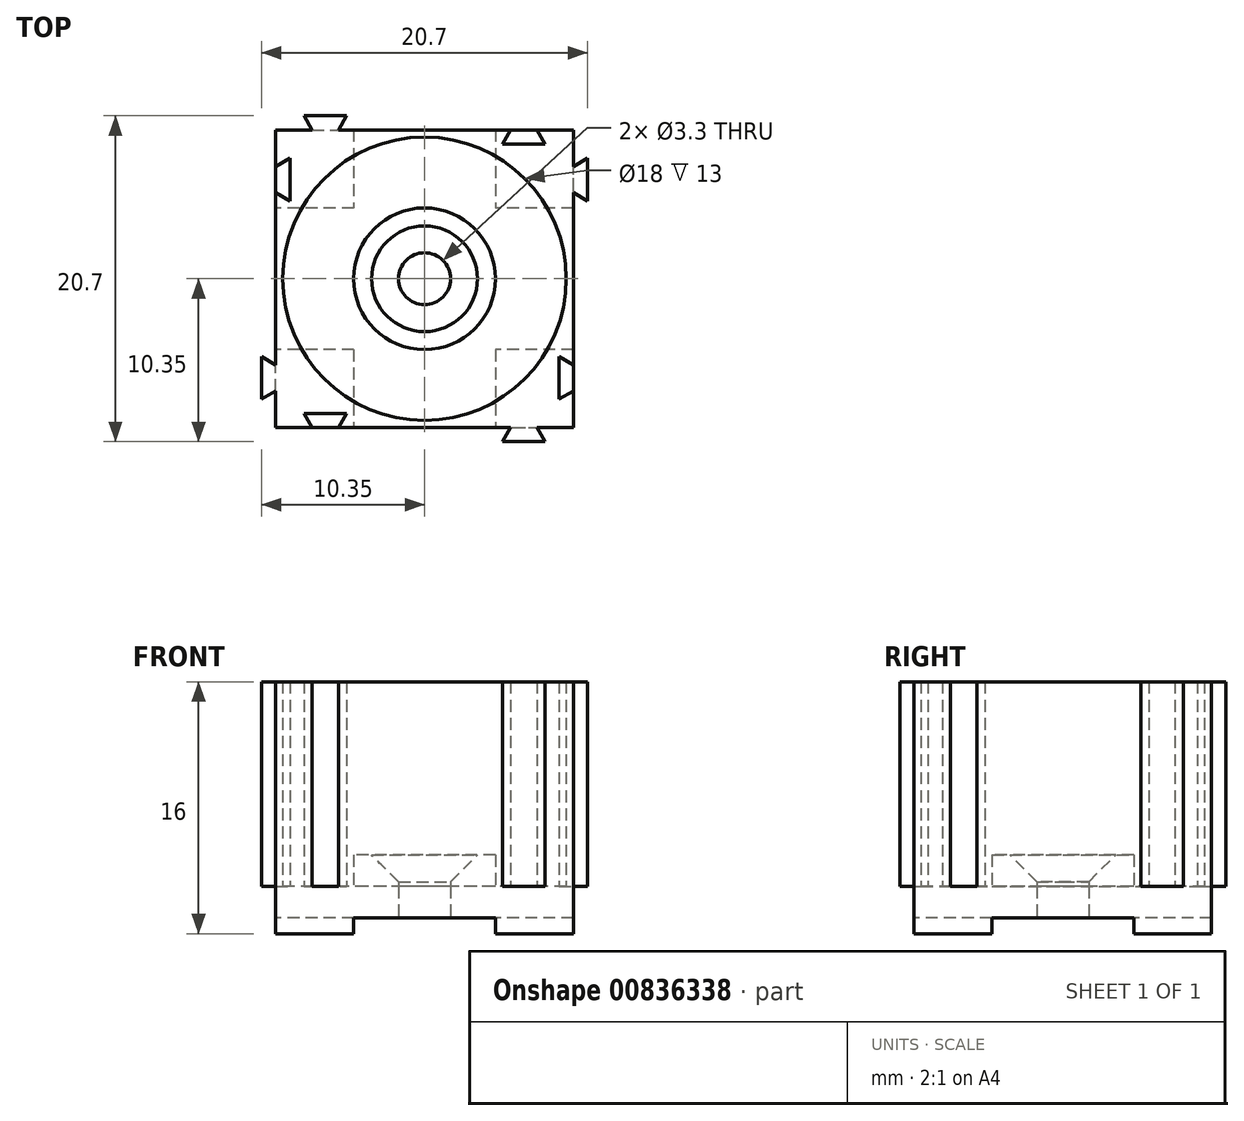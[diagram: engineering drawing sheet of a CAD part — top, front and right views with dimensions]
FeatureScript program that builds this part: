
annotation { "Feature Type Name" : "Feature", "Feature Type Description" : "" }
export const myFeature = defineFeature(function(context is Context, id is Id, definition is map)
    precondition{}
    {
        {
            assignVariable(context, id + "F0", {"name" : "Height", "anyValue" : 65});
        }
        {
            var Q0;
            Q0=qCreatedBy(makeId("Top.planeOp"),FACE);
            var sketch = newSketch(context, id + "F1", { "sketchPlane" : qUnion([Q0])});
            skCircle(sketch, "E0", {"center": v(0, 0) * mm, "radius": 9 * mm});
            skLineSegment(sketch, "E1.bottom", {"start": v(9.45, -9.45) * mm, "end": v(7.13, -9.45) * mm});
            skLineSegment(sketch, "E1.top", {"start": v(9.45, 9.45) * mm, "end": v(7.13, 9.45) * mm});
            skLineSegment(sketch, "E1.left", {"start": v(9.45, -9.45) * mm, "end": v(9.45, -7.13) * mm});
            skLineSegment(sketch, "E1.right", {"start": v(-9.45, -9.45) * mm, "end": v(-9.45, -7.13) * mm});
            skLineSegment(sketch, "E2", {"start": v(5.47, 9.45) * mm, "end": v(4.95, 8.55) * mm});
            skLineSegment(sketch, "E3", {"start": v(4.95, 8.55) * mm, "end": v(7.65, 8.55) * mm});
            skLineSegment(sketch, "E4", {"start": v(7.65, 8.55) * mm, "end": v(7.13, 9.45) * mm});
            skLineSegment(sketch, "E5", {"start": v(-7.13, 9.45) * mm, "end": v(-7.65, 10.35) * mm});
            skLineSegment(sketch, "E6", {"start": v(-7.65, 10.35) * mm, "end": v(-4.95, 10.35) * mm});
            skLineSegment(sketch, "E7", {"start": v(-4.95, 10.35) * mm, "end": v(-5.47, 9.45) * mm});
            skLineSegment(sketch, "E8", {"start": v(-6.3, 10.35) * mm, "end": v(-6.3, -11.64) * mm, "construction": true});
            skLineSegment(sketch, "E9", {"start": v(6.3, 8.55) * mm, "end": v(6.3, -11.89) * mm, "construction": true});
            skLineSegment(sketch, "E10", {"start": v(0, 9.45) * mm, "end": v(0, -9.45) * mm, "construction": true});
            skLineSegment(sketch, "E11.trimOffspring", {"start": v(-7.13, 9.45) * mm, "end": v(-9.45, 9.45) * mm});
            skLineSegment(sketch, "E12.trimOffspring", {"start": v(5.47, 9.45) * mm, "end": v(-5.47, 9.45) * mm});
            skLineSegment(sketch, "E13", {"start": v(-7.13, -9.45) * mm, "end": v(-7.65, -8.55) * mm});
            skLineSegment(sketch, "E14", {"start": v(-7.65, -8.55) * mm, "end": v(-4.95, -8.55) * mm});
            skLineSegment(sketch, "E15", {"start": v(-4.95, -8.55) * mm, "end": v(-5.47, -9.45) * mm});
            skLineSegment(sketch, "E16", {"start": v(5.47, -9.45) * mm, "end": v(4.95, -10.35) * mm});
            skLineSegment(sketch, "E17", {"start": v(4.95, -10.35) * mm, "end": v(7.65, -10.35) * mm});
            skLineSegment(sketch, "E18", {"start": v(7.65, -10.35) * mm, "end": v(7.13, -9.45) * mm});
            skLineSegment(sketch, "E19.trimOffspring", {"start": v(5.47, -9.45) * mm, "end": v(-5.47, -9.45) * mm});
            skLineSegment(sketch, "E20.trimOffspring", {"start": v(-7.13, -9.45) * mm, "end": v(-9.45, -9.45) * mm});
            skLineSegment(sketch, "E21", {"start": v(13.55, 6.3) * mm, "end": v(-13.25, 6.3) * mm, "construction": true});
            skLineSegment(sketch, "E22", {"start": v(14.02, -6.3) * mm, "end": v(-13.91, -6.3) * mm, "construction": true});
            skLineSegment(sketch, "E23", {"start": v(9.45, 0) * mm, "end": v(-9.45, 0) * mm, "construction": true});
            skPoint(sketch, "E24", {"position": v(-6.3, -8.55) * mm});
            skLineSegment(sketch, "E25", {"start": v(9.45, 7.13) * mm, "end": v(10.35, 7.65) * mm});
            skLineSegment(sketch, "E26", {"start": v(10.35, 7.65) * mm, "end": v(10.35, 4.95) * mm});
            skLineSegment(sketch, "E27", {"start": v(10.35, 4.95) * mm, "end": v(9.45, 5.47) * mm});
            skLineSegment(sketch, "E28.trimOffspring", {"start": v(9.45, 7.13) * mm, "end": v(9.45, 9.45) * mm});
            skLineSegment(sketch, "E29", {"start": v(9.45, -5.47) * mm, "end": v(8.55, -4.95) * mm});
            skLineSegment(sketch, "E30", {"start": v(8.55, -4.95) * mm, "end": v(8.55, -7.65) * mm});
            skLineSegment(sketch, "E31", {"start": v(8.55, -7.65) * mm, "end": v(9.45, -7.13) * mm});
            skLineSegment(sketch, "E32.trimOffspring", {"start": v(9.45, -5.47) * mm, "end": v(9.45, 5.47) * mm});
            skLineSegment(sketch, "E33", {"start": v(-9.45, -5.47) * mm, "end": v(-10.35, -4.95) * mm});
            skLineSegment(sketch, "E34", {"start": v(-10.35, -4.95) * mm, "end": v(-10.35, -7.65) * mm});
            skLineSegment(sketch, "E35", {"start": v(-10.35, -7.65) * mm, "end": v(-9.45, -7.13) * mm});
            skLineSegment(sketch, "E36", {"start": v(-9.45, 7.13) * mm, "end": v(-8.55, 7.65) * mm});
            skLineSegment(sketch, "E37", {"start": v(-8.55, 7.65) * mm, "end": v(-8.55, 4.95) * mm});
            skLineSegment(sketch, "E38", {"start": v(-8.55, 4.95) * mm, "end": v(-9.45, 5.47) * mm});
            skLineSegment(sketch, "E39.trimOffspring", {"start": v(-9.45, -5.47) * mm, "end": v(-9.45, 5.47) * mm});
            skLineSegment(sketch, "E40.trimOffspring", {"start": v(-9.45, 7.13) * mm, "end": v(-9.45, 9.45) * mm});
            skSolve(sketch);
        }
        {
            var Q0;
            Q0=makeQuery(id+"F1.imprint","IMPRINT",FACE,{"disambiguationData":[TD([[makeQuery(id+"F1.imprint","IMPRINT",EDGE,{"derivedFrom":sQuery(id+"F1.wireOp",EDGE,"E0")}),-1.0]])]});
            extrude(context, id + "F2", {"entities" : qUnion([Q0]), "depth" : (getVariable(context, 'Height') * 0.2) * mm, "offsetDistance" : 25 * mm});
        }
        {
            var Q0;
            Q0=makeQuery(id+"F2.opExtrude","CAP_FACE",FACE,{"disambiguationData":[OSD([sQuery(id+"F1.wireOp",EDGE,"E0"),sQuery(id+"F1.wireOp",EDGE,"E1.bottom"),sQuery(id+"F1.wireOp",EDGE,"E1.top"),sQuery(id+"F1.wireOp",EDGE,"E1.left"),sQuery(id+"F1.wireOp",EDGE,"E1.right"),sQuery(id+"F1.wireOp",EDGE,"E2"),sQuery(id+"F1.wireOp",EDGE,"E3"),sQuery(id+"F1.wireOp",EDGE,"E4"),sQuery(id+"F1.wireOp",EDGE,"E5"),sQuery(id+"F1.wireOp",EDGE,"E6"),sQuery(id+"F1.wireOp",EDGE,"E7"),sQuery(id+"F1.wireOp",EDGE,"E11.trimOffspring"),sQuery(id+"F1.wireOp",EDGE,"E12.trimOffspring"),sQuery(id+"F1.wireOp",EDGE,"E13"),sQuery(id+"F1.wireOp",EDGE,"E14"),sQuery(id+"F1.wireOp",EDGE,"E15"),sQuery(id+"F1.wireOp",EDGE,"E16"),sQuery(id+"F1.wireOp",EDGE,"E17"),sQuery(id+"F1.wireOp",EDGE,"E18"),sQuery(id+"F1.wireOp",EDGE,"E19.trimOffspring"),sQuery(id+"F1.wireOp",EDGE,"E20.trimOffspring"),sQuery(id+"F1.wireOp",EDGE,"E25"),sQuery(id+"F1.wireOp",EDGE,"E26"),sQuery(id+"F1.wireOp",EDGE,"E27"),sQuery(id+"F1.wireOp",EDGE,"E28.trimOffspring"),sQuery(id+"F1.wireOp",EDGE,"E29"),sQuery(id+"F1.wireOp",EDGE,"E30"),sQuery(id+"F1.wireOp",EDGE,"E31"),sQuery(id+"F1.wireOp",EDGE,"E32.trimOffspring"),sQuery(id+"F1.wireOp",EDGE,"E33"),sQuery(id+"F1.wireOp",EDGE,"E34"),sQuery(id+"F1.wireOp",EDGE,"E35"),sQuery(id+"F1.wireOp",EDGE,"E36"),sQuery(id+"F1.wireOp",EDGE,"E37"),sQuery(id+"F1.wireOp",EDGE,"E38"),sQuery(id+"F1.wireOp",EDGE,"E39.trimOffspring"),sQuery(id+"F1.wireOp",EDGE,"E40.trimOffspring")])],"isStart":true});
            var sketch = newSketch(context, id + "F3", { "sketchPlane" : qUnion([Q0])});
            skLineSegment(sketch, "E41.bottom", {"start": v(-9.45, 9.45) * mm, "end": v(9.45, 9.45) * mm});
            skLineSegment(sketch, "E41.top", {"start": v(-9.45, -9.45) * mm, "end": v(9.45, -9.45) * mm});
            skLineSegment(sketch, "E41.left", {"start": v(-9.45, 9.45) * mm, "end": v(-9.45, -9.45) * mm});
            skLineSegment(sketch, "E41.right", {"start": v(9.45, 9.45) * mm, "end": v(9.45, -9.45) * mm});
            skSolve(sketch);
        }
        {
            var Q0;
            Q0 = qSketchRegion(id + "F3", true);
            extrude(context, id + "F4", {"entities" : qUnion([Q0]), "operationType" : NewBodyOperationType.ADD, "depth" : 3 * mm, "offsetDistance" : 25 * mm});
        }
        {
            var Q0;
            Q0=makeQuery(id+"F4.boolean.opBoolean","SPLIT",FACE,{"disambiguationData":[TD([makeQuery(id+"F2.opExtrude","SWEPT_FACE",FACE,{"disambiguationData":[OSD([sQuery(id+"F1.wireOp",EDGE,"E0")])]})])],"derivedFrom":makeQuery(id+"F4.opExtrude","CAP_FACE",FACE,{"disambiguationData":[OSD([sQuery(id+"F3.wireOp",EDGE,"E41.bottom"),sQuery(id+"F3.wireOp",EDGE,"E41.top"),sQuery(id+"F3.wireOp",EDGE,"E41.left"),sQuery(id+"F3.wireOp",EDGE,"E41.right")])],"isStart":true})});
            var sketch = newSketch(context, id + "F5", { "sketchPlane" : qUnion([Q0])});
            skCircle(sketch, "E42", {"center": v(0, 0) * mm, "radius": 4.5 * mm});
            skSolve(sketch);
        }
        {
            var Q0;
            Q0=makeQuery(id+"F5.imprint","IMPRINT",FACE,{"disambiguationData":[TD([[makeQuery(id+"F5.imprint","IMPRINT",EDGE,{"derivedFrom":sQuery(id+"F5.wireOp",EDGE,"E42")}),1.0]])]});
            extrude(context, id + "F6", {"entities" : qUnion([Q0]), "depth" : 2 * mm, "offsetDistance" : 25 * mm});
        }
        {
            var Q0;
            Q0=makeQuery(id+"F4.opExtrude","CAP_FACE",FACE,{"disambiguationData":[OSD([sQuery(id+"F3.wireOp",EDGE,"E41.bottom"),sQuery(id+"F3.wireOp",EDGE,"E41.top"),sQuery(id+"F3.wireOp",EDGE,"E41.left"),sQuery(id+"F3.wireOp",EDGE,"E41.right")])],"isStart":false});
            var sketch = newSketch(context, id + "F7", { "sketchPlane" : qUnion([Q0])});
            skLineSegment(sketch, "E43.bottom", {"start": v(4.5, -9.45) * mm, "end": v(-4.5, -9.45) * mm});
            skLineSegment(sketch, "E43.top", {"start": v(4.5, 9.45) * mm, "end": v(-4.5, 9.45) * mm});
            skLineSegment(sketch, "E43.left", {"start": v(4.5, -9.45) * mm, "end": v(4.5, -4.5) * mm});
            skLineSegment(sketch, "E43.right", {"start": v(-4.5, -9.45) * mm, "end": v(-4.5, -4.5) * mm});
            skPoint(sketch, "E43.middle", {"position": v(0, 0) * mm});
            skLineSegment(sketch, "E44.bottom", {"start": v(9.45, -4.5) * mm, "end": v(4.5, -4.5) * mm});
            skLineSegment(sketch, "E44.top", {"start": v(9.45, 4.5) * mm, "end": v(4.5, 4.5) * mm});
            skLineSegment(sketch, "E44.left", {"start": v(9.45, -4.5) * mm, "end": v(9.45, 4.5) * mm});
            skLineSegment(sketch, "E44.right", {"start": v(-9.45, -4.5) * mm, "end": v(-9.45, 4.5) * mm});
            skLineSegment(sketch, "E45.trimOffspring", {"start": v(-4.5, 4.5) * mm, "end": v(-4.5, 9.45) * mm});
            skLineSegment(sketch, "E46.trimOffspring", {"start": v(-4.5, 4.5) * mm, "end": v(-9.45, 4.5) * mm});
            skLineSegment(sketch, "E47.trimOffspring", {"start": v(4.5, 4.5) * mm, "end": v(4.5, 9.45) * mm});
            skLineSegment(sketch, "E48.trimOffspring", {"start": v(-4.5, -4.5) * mm, "end": v(-9.45, -4.5) * mm});
            skSolve(sketch);
        }
        {
            var Q0;
            Q0 = qSketchRegion(id + "F7", true);
            extrude(context, id + "F8", {"entities" : qUnion([Q0]), "operationType" : NewBodyOperationType.REMOVE, "oppositeDirection" : true, "depth" : 1 * mm, "offsetDistance" : 25 * mm});
        }
        {
            var Q0;
            Q0=makeQuery(id+"F6.opExtrude","CAP_FACE",FACE,{"disambiguationData":[OSD([sQuery(id+"F5.wireOp",EDGE,"E42")])],"isStart":false});
            var sketch = newSketch(context, id + "F9", { "sketchPlane" : qUnion([Q0])});
            skPoint(sketch, "E49", {"position": v(0, 0) * mm});
            skSolve(sketch);
        }
        {
            var Q0;
            Q0=sQuery(id+"F9.wireOp",VERTEX,"E49");
            var Q1;
            Q1=makeQuery(id+"F2.opExtrude","SWEPT_BODY",BODY,{"disambiguationData":[OSD([sQuery(id+"F1.wireOp",EDGE,"E0"),sQuery(id+"F1.wireOp",EDGE,"E1.bottom"),sQuery(id+"F1.wireOp",EDGE,"E1.top"),sQuery(id+"F1.wireOp",EDGE,"E1.left"),sQuery(id+"F1.wireOp",EDGE,"E1.right"),sQuery(id+"F1.wireOp",EDGE,"E2"),sQuery(id+"F1.wireOp",EDGE,"E3"),sQuery(id+"F1.wireOp",EDGE,"E4"),sQuery(id+"F1.wireOp",EDGE,"E5"),sQuery(id+"F1.wireOp",EDGE,"E6"),sQuery(id+"F1.wireOp",EDGE,"E7"),sQuery(id+"F1.wireOp",EDGE,"E11.trimOffspring"),sQuery(id+"F1.wireOp",EDGE,"E12.trimOffspring"),sQuery(id+"F1.wireOp",EDGE,"E13"),sQuery(id+"F1.wireOp",EDGE,"E14"),sQuery(id+"F1.wireOp",EDGE,"E15"),sQuery(id+"F1.wireOp",EDGE,"E16"),sQuery(id+"F1.wireOp",EDGE,"E17"),sQuery(id+"F1.wireOp",EDGE,"E18"),sQuery(id+"F1.wireOp",EDGE,"E19.trimOffspring"),sQuery(id+"F1.wireOp",EDGE,"E20.trimOffspring"),sQuery(id+"F1.wireOp",EDGE,"E25"),sQuery(id+"F1.wireOp",EDGE,"E26"),sQuery(id+"F1.wireOp",EDGE,"E27"),sQuery(id+"F1.wireOp",EDGE,"E28.trimOffspring"),sQuery(id+"F1.wireOp",EDGE,"E29"),sQuery(id+"F1.wireOp",EDGE,"E30"),sQuery(id+"F1.wireOp",EDGE,"E31"),sQuery(id+"F1.wireOp",EDGE,"E32.trimOffspring"),sQuery(id+"F1.wireOp",EDGE,"E33"),sQuery(id+"F1.wireOp",EDGE,"E34"),sQuery(id+"F1.wireOp",EDGE,"E35"),sQuery(id+"F1.wireOp",EDGE,"E36"),sQuery(id+"F1.wireOp",EDGE,"E37"),sQuery(id+"F1.wireOp",EDGE,"E38"),sQuery(id+"F1.wireOp",EDGE,"E39.trimOffspring"),sQuery(id+"F1.wireOp",EDGE,"E40.trimOffspring")])]});
            var Q2;
            Q2=makeQuery(id+"F6.opExtrude","SWEPT_BODY",BODY,{"disambiguationData":[OSD([sQuery(id+"F5.wireOp",EDGE,"E42")])]});
            hole(context, id + "F10", {"style" : HoleStyle.C_SINK, "endStyle" : HoleEndStyle.THROUGH, "standardTappedOrClearance" : lookupTablePath({ "fit" : "Normal", "standard" : "ISO", "size" : "M3", "type" : "Clearance" }), "standardBlindInLast" : lookupTablePath({ "fit" : "Standard", "standard" : "ISO", "size" : "M3", "type" : "Clearance" }), "holeDiameter" : 3.3 * mm, "cSinkDiameter" : 6.72 * mm, "cSinkAngle" : 90 * degree, "majorDiameter" : 5 * mm, "isTappedThrough" : true, "tappedDepth" : 7.5 * mm, "tapClearance" : 3, "locations" : qUnion([Q0]), "scope" : qUnion([Q1, Q2]), "startStyle" : HoleStartStyle.PART});
        }
    });
